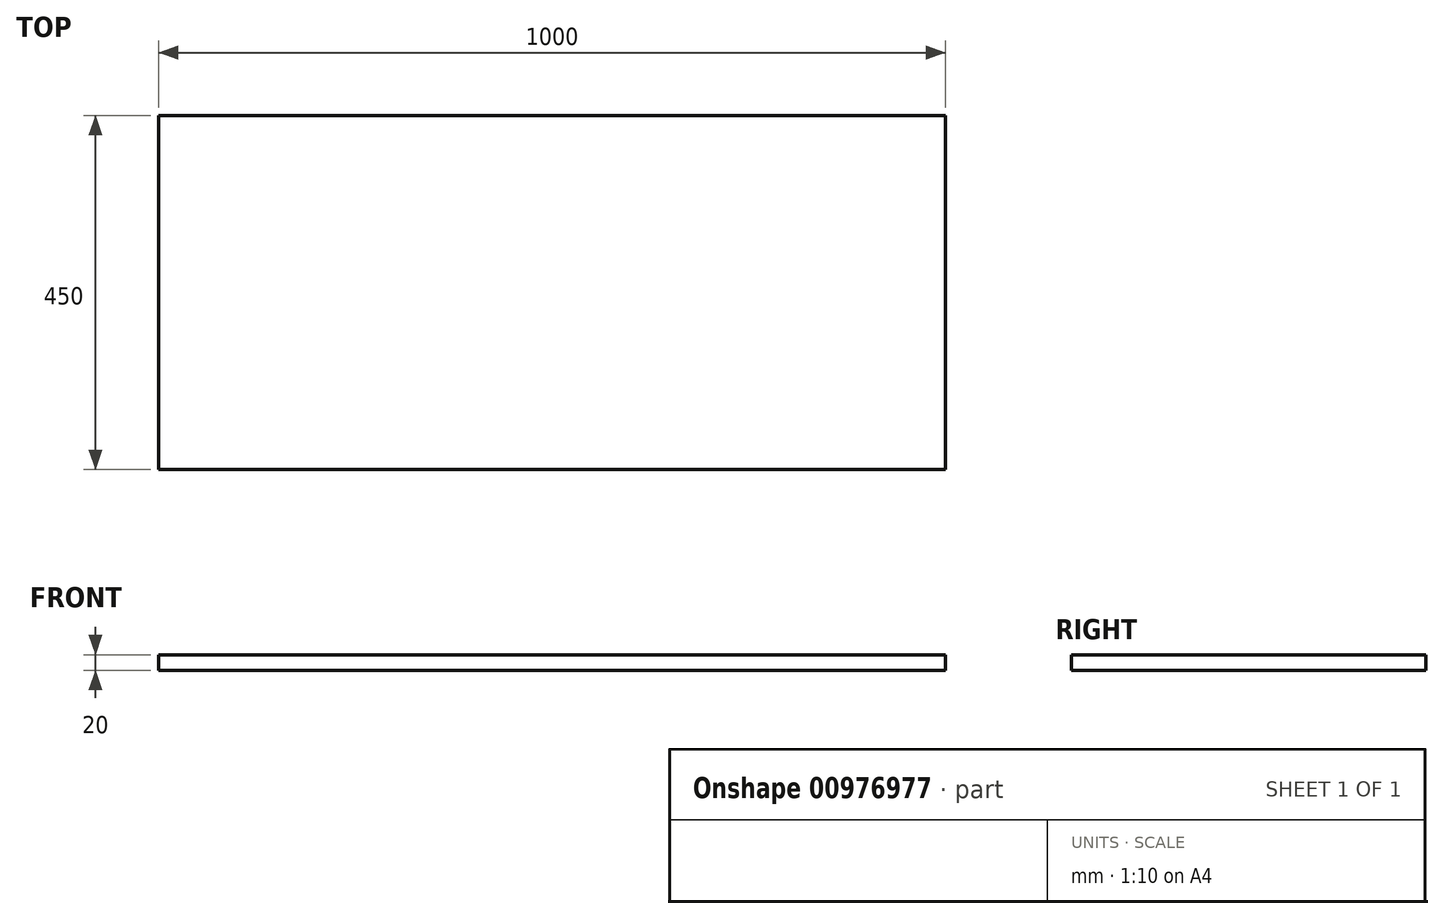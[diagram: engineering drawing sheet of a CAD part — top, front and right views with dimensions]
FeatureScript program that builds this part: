
annotation { "Feature Type Name" : "Feature", "Feature Type Description" : "" }
export const myFeature = defineFeature(function(context is Context, id is Id, definition is map)
    precondition{}
    {
        {
            var Q0;
            Q0=qCreatedBy(makeId("Top.planeOp"),FACE);
            var sketch = newSketch(context, id + "F0", { "sketchPlane" : qUnion([Q0])});
            skLineSegment(sketch, "E0.bottom", {"start": v(500, 225) * mm, "end": v(-500, 225) * mm});
            skLineSegment(sketch, "E0.top", {"start": v(500, -225) * mm, "end": v(-500, -225) * mm});
            skLineSegment(sketch, "E0.left", {"start": v(500, 225) * mm, "end": v(500, -225) * mm});
            skLineSegment(sketch, "E0.right", {"start": v(-500, 225) * mm, "end": v(-500, -225) * mm});
            skPoint(sketch, "E0.middle", {"position": v(0, 0) * mm});
            skSolve(sketch);
        }
        {
            var Q0;
            Q0 = qSketchRegion(id + "F0", true);
            extrude(context, id + "F1", {"entities" : qUnion([Q0]), "depth" : 20 * mm, "offsetDistance" : 25 * mm});
        }
    });
